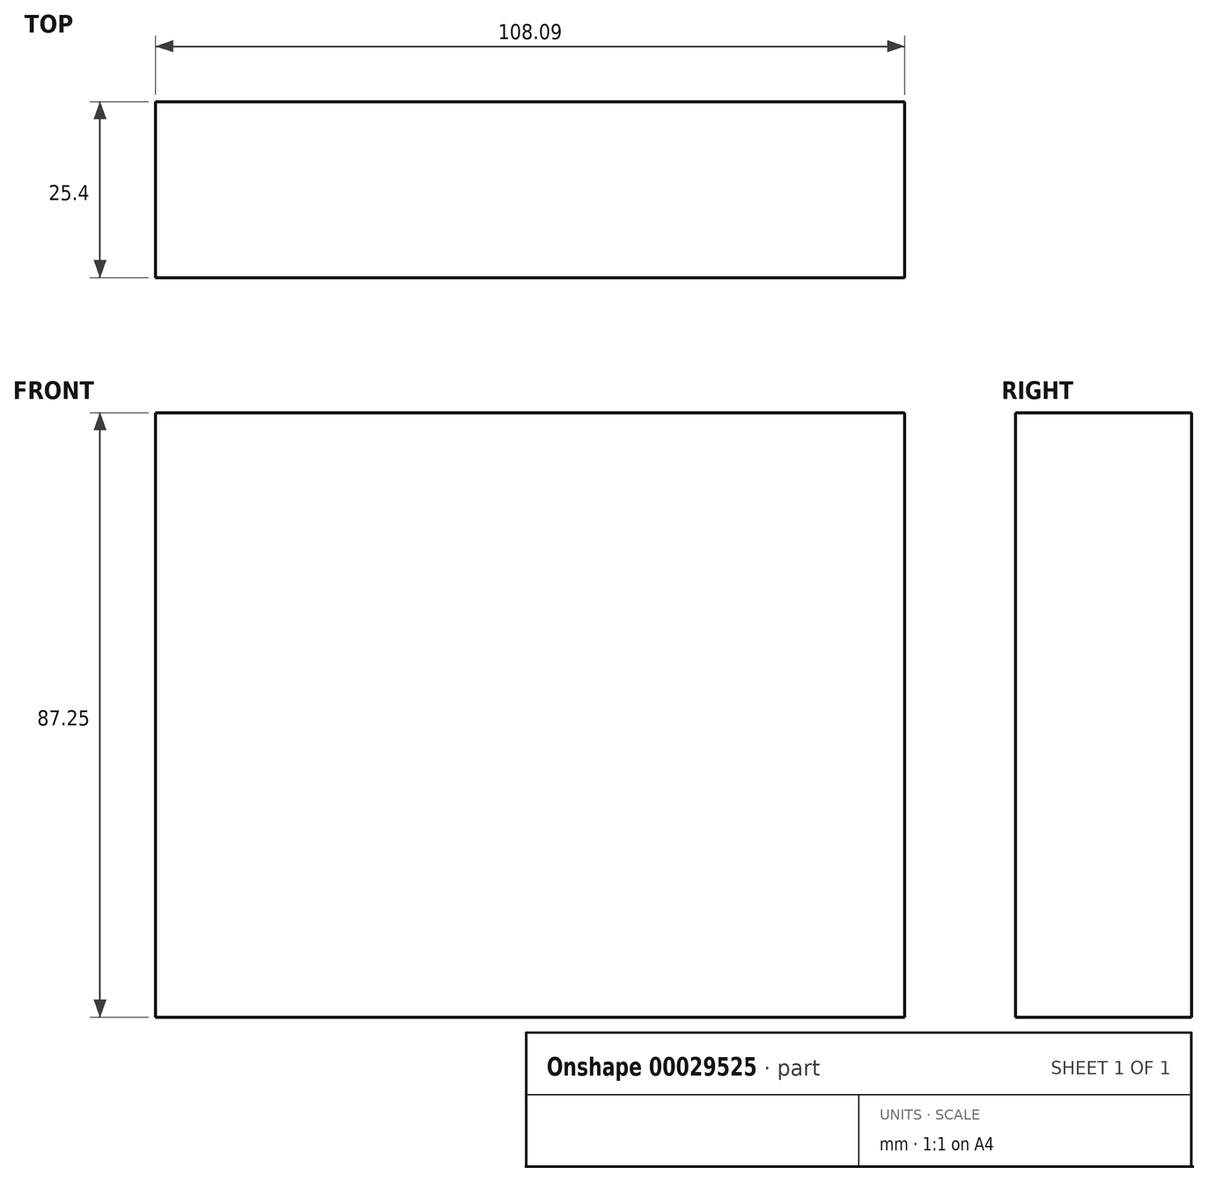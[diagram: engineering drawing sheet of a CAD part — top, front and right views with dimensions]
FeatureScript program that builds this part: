
annotation { "Feature Type Name" : "Feature", "Feature Type Description" : "" }
export const myFeature = defineFeature(function(context is Context, id is Id, definition is map)
    precondition{}
    {
        {
            var Q0;
            Q0=qCreatedBy(makeId("Front.planeOp"),FACE);
            var sketch = newSketch(context, id + "F0", { "sketchPlane" : qUnion([Q0])});
            skLineSegment(sketch, "E0.bottom", {"start": v(-56.17, 40.83) * mm, "end": v(51.92, 40.83) * mm});
            skLineSegment(sketch, "E0.top", {"start": v(-56.17, -46.42) * mm, "end": v(51.92, -46.42) * mm});
            skLineSegment(sketch, "E0.left", {"start": v(-56.17, 40.83) * mm, "end": v(-56.17, -46.42) * mm});
            skLineSegment(sketch, "E0.right", {"start": v(51.92, 40.83) * mm, "end": v(51.92, -46.42) * mm});
            skSolve(sketch);
        }
        {
            var Q0;
            Q0=makeQuery(id+"F0.imprint","IMPRINT",FACE,{"disambiguationData":[TD([[makeQuery(id+"F0.imprint","IMPRINT",EDGE,{"derivedFrom":sQuery(id+"F0.wireOp",EDGE,"E0.bottom")}),-1.0]])]});
            extrude(context, id + "F1", {"entities" : qUnion([Q0]), "depth" : 25.4 * mm});
        }
    });
